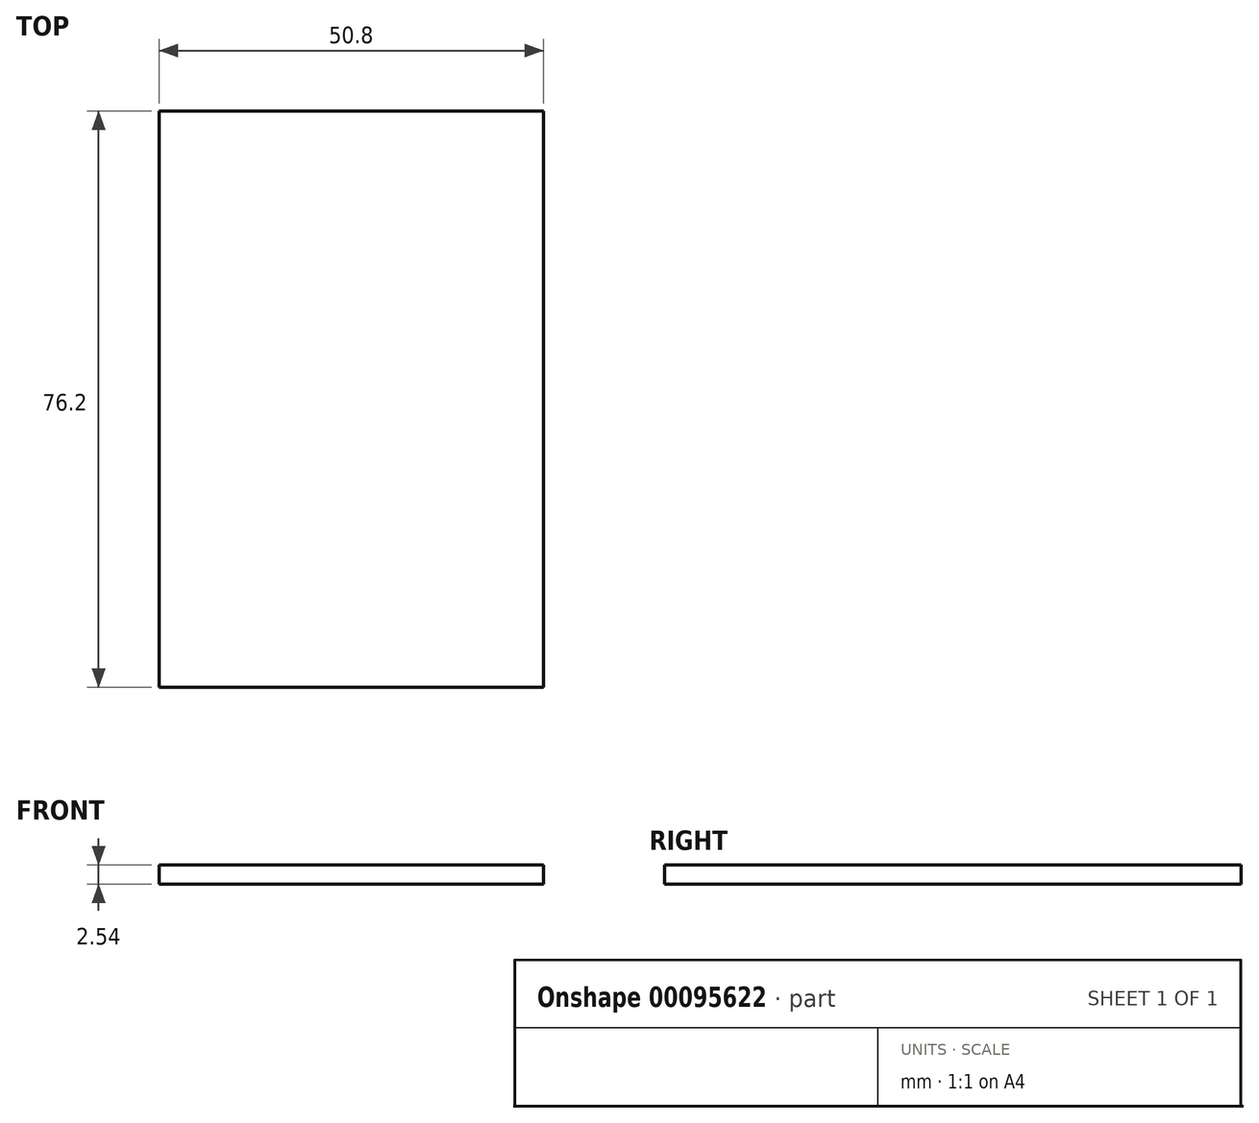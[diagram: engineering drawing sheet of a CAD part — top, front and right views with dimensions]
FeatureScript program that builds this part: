
annotation { "Feature Type Name" : "Feature", "Feature Type Description" : "" }
export const myFeature = defineFeature(function(context is Context, id is Id, definition is map)
    precondition{}
    {
        {
            var Q0;
            Q0=qCreatedBy(makeId("Top.planeOp"),FACE);
            var sketch = newSketch(context, id + "F0", { "sketchPlane" : qUnion([Q0])});
            skLineSegment(sketch, "E0.bottom", {"start": v(0, 0) * mm, "end": v(50.8, 0) * mm});
            skLineSegment(sketch, "E0.top", {"start": v(0, -76.2) * mm, "end": v(50.8, -76.2) * mm});
            skLineSegment(sketch, "E0.left", {"start": v(0, 0) * mm, "end": v(0, -76.2) * mm});
            skLineSegment(sketch, "E0.right", {"start": v(50.8, 0) * mm, "end": v(50.8, -76.2) * mm});
            skSolve(sketch);
        }
        {
            var Q0;
            Q0 = qSketchRegion(id + "F0", true);
            extrude(context, id + "F1", {"entities" : qUnion([Q0]), "depth" : 2.54 * mm});
        }
    });
